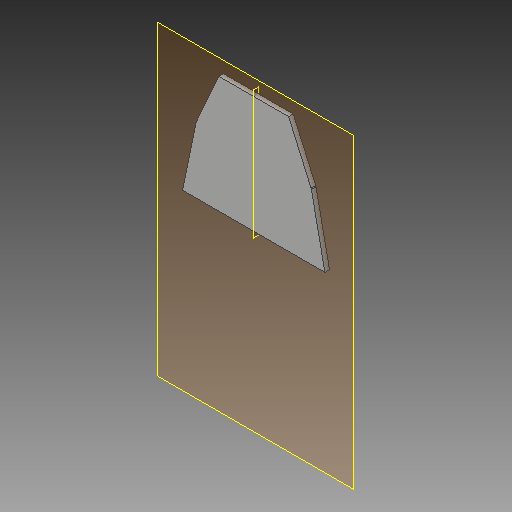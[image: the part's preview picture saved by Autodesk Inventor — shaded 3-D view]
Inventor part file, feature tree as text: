
AUTODESK INVENTOR PART (.ipt)
format: ipt  version: 2018 (Build 220112000, 112)  size: 155,648 bytes
history: native  units: mm
features: other x8, plane x1, sheet_metal_op x1, sketch x1, projected_geometry x1
ambient origin geometry x8: Origin, YZ Plane, XZ Plane, XY Plane, X Axis, Y Axis, Z Axis, Center Point
bodies: Solid1 (feature_tree)
feature tree (12):
  plane  "Work Plane1"
  sheet_metal_op  "Face1"
  other  "modplan parallel med plade"
  other  "midtplan"
  other  "Plate1"
  sketch  "Sketch3"  dims[d3=88.078826mm d4=44.039413mm d8=3.0mm d12=80.0mm d14=2.0mm d15=3.0mm d16=0.0mm]
  projected_geometry  "Projected Loop2"
  other  "2 mm mindre"
  parser-record x1  (decoder bookkeeping rows leaked as tree rows — omitted from the tree; the rows remain in map.json)
  other  "modul.iam"
  other  "stilladssøjle:1"
  other  "rør:1"
note: 1 file-system path scrubbed to <path> (originals preserved in map.json)
